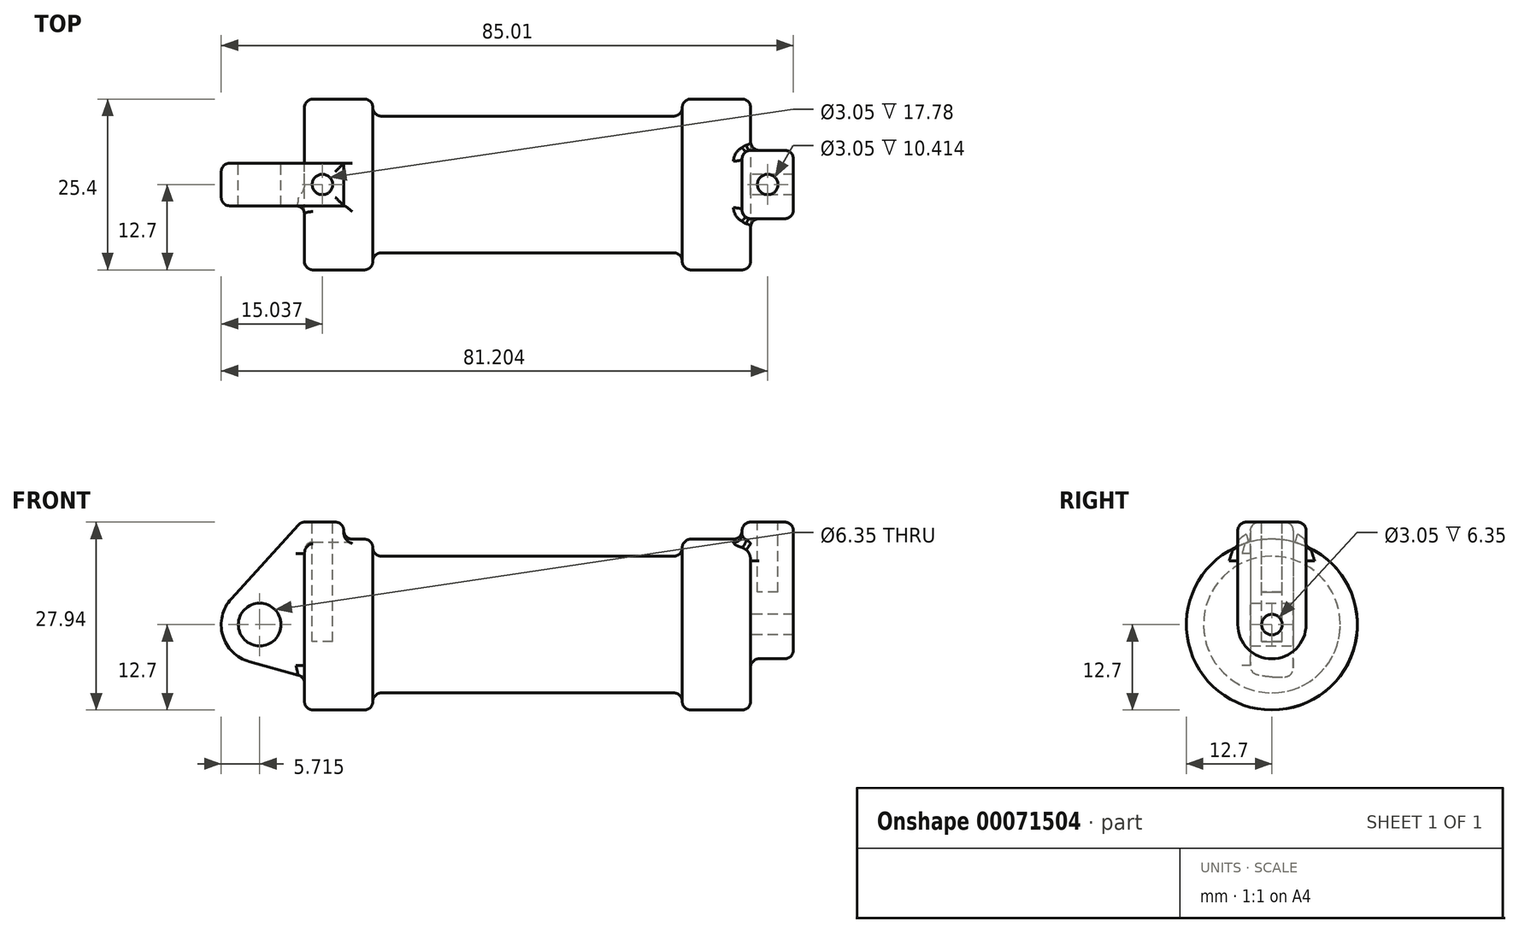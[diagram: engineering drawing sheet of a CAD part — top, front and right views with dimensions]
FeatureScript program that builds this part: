
annotation { "Feature Type Name" : "Feature", "Feature Type Description" : "" }
export const myFeature = defineFeature(function(context is Context, id is Id, definition is map)
    precondition{}
    {
        {
            var Q0;
            Q0=qCreatedBy(makeId("Front.planeOp"),FACE);
            var sketch = newSketch(context, id + "F0", { "sketchPlane" : qUnion([Q0])});
            skLineSegment(sketch, "E0", {"start": v(0, 0) * mm, "end": v(0, 12.7) * mm});
            skLineSegment(sketch, "E1", {"start": v(0, 12.7) * mm, "end": v(10.16, 12.7) * mm});
            skLineSegment(sketch, "E2", {"start": v(10.16, 12.7) * mm, "end": v(10.16, 10.16) * mm});
            skLineSegment(sketch, "E3", {"start": v(10.16, 10.16) * mm, "end": v(56.13, 10.16) * mm});
            skLineSegment(sketch, "E4", {"start": v(56.13, 10.16) * mm, "end": v(56.13, 12.7) * mm});
            skLineSegment(sketch, "E5", {"start": v(56.13, 12.7) * mm, "end": v(66.3, 12.7) * mm});
            skLineSegment(sketch, "E6", {"start": v(66.3, 12.7) * mm, "end": v(66.3, 0) * mm});
            skLineSegment(sketch, "E7", {"start": v(66.3, 0) * mm, "end": v(0, 0) * mm});
            skLineSegment(sketch, "E8", {"start": v(5.84, 15.24) * mm, "end": v(-0.5, 15.24) * mm});
            skLineSegment(sketch, "E9", {"start": v(-0.5, 15.24) * mm, "end": v(-10.88, 3.85) * mm});
            skLineSegment(sketch, "E10", {"start": v(0, 0) * mm, "end": v(-6.65, 0) * mm});
            skCircle(sketch, "E11", {"center": v(-6.65, 0) * mm, "radius": 5.72 * mm});
            skCircle(sketch, "E12", {"center": v(-6.65, 0) * mm, "radius": 3.18 * mm});
            skLineSegment(sketch, "E13", {"start": v(5.84, 15.24) * mm, "end": v(5.84, -9.4) * mm});
            skLineSegment(sketch, "E14", {"start": v(5.84, -9.4) * mm, "end": v(-8.18, -5.5) * mm});
            skSolve(sketch);
        }
        {
            var Q0;
            {var subQ0=sQuery(id+"F0.wireOp",EDGE,"E2");Q0=makeQuery(id+"F0.imprint","IMPRINT",FACE,{"disambiguationData":[TD([[makeQuery(id+"F0.imprint","IMPRINT",EDGE,{"derivedFrom":subQ0}),-1.0]])]});}
            var Q1;
            {var subQ0=sQuery(id+"F0.wireOp",EDGE,"E0");Q1=makeQuery(id+"F0.imprint","IMPRINT",FACE,{"disambiguationData":[TD([[makeQuery(id+"F0.imprint","IMPRINT",EDGE,{"derivedFrom":subQ0}),-1.0]])]});}
            var Q2;
            Q2=sQuery(id+"F0.wireOp",EDGE,"E7");
            revolve(context, id + "F1", {"entities" : qUnion([Q0, Q1]), "axis" : qUnion([Q2]), "revolveType" : RevolveType.FULL});
        }
        {
            var Q0;
            {var subQ3=sQuery(id+"F0.wireOp",EDGE,"E0");Q0=makeQuery(id+"F0.imprint","IMPRINT",FACE,{"disambiguationData":[TD([[makeQuery(id+"F0.imprint","IMPRINT",EDGE,{"derivedFrom":subQ3}),1.0]])]});}
            var Q1;
            {var subQ0=sQuery(id+"F0.wireOp",EDGE,"E14");Q1=makeQuery(id+"F0.imprint","IMPRINT",FACE,{"disambiguationData":[TD([[makeQuery(id+"F0.imprint","IMPRINT",EDGE,{"derivedFrom":subQ0}),-1.0]])]});}
            var Q2;
            {var subQ4=sQuery(id+"F0.wireOp",EDGE,"E12");Q2=makeQuery(id+"F0.imprint","IMPRINT",FACE,{"disambiguationData":[TD([[makeQuery(id+"F0.imprint","IMPRINT",EDGE,{"derivedFrom":subQ4}),-1.0]])]});}
            var Q3;
            {var subQ0=sQuery(id+"F0.wireOp",EDGE,"E0");Q3=makeQuery(id+"F0.imprint","IMPRINT",FACE,{"disambiguationData":[TD([[makeQuery(id+"F0.imprint","IMPRINT",EDGE,{"derivedFrom":subQ0}),-1.0]])]});}
            extrude(context, id + "F2", {"entities" : qUnion([Q0, Q1, Q2, Q3]), "operationType" : NewBodyOperationType.ADD, "endBound" : BoundingType.SYMMETRIC, "depth" : 6.35 * mm});
        }
        {
            var Q0;
            Q0=makeQuery(id+"F1.opRevolve","SWEPT_FACE",FACE,{"disambiguationData":[OSD([sQuery(id+"F0.wireOp",EDGE,"E6")])]});
            var sketch = newSketch(context, id + "F3", { "sketchPlane" : qUnion([Q0])});
            skCircle(sketch, "E15", {"center": v(0, 0) * mm, "radius": 1.52 * mm});
            skCircle(sketch, "E16", {"center": v(0, 0) * mm, "radius": 5.08 * mm});
            skLineSegment(sketch, "E17", {"start": v(5.08, 0) * mm, "end": v(5.08, 15.24) * mm});
            skLineSegment(sketch, "E18", {"start": v(-5.08, 0) * mm, "end": v(-5.08, 15.24) * mm});
            skLineSegment(sketch, "E19", {"start": v(-5.08, 15.24) * mm, "end": v(5.08, 15.24) * mm});
            skSolve(sketch);
        }
        {
            var Q0;
            {var subQ0=sQuery(id+"F3.wireOp",EDGE,"E19");Q0=makeQuery(id+"F3.imprint","IMPRINT",FACE,{"disambiguationData":[TD([[makeQuery(id+"F3.imprint","IMPRINT",EDGE,{"derivedFrom":subQ0}),-1.0]])]});}
            var Q1;
            {var subQ0=sQuery(id+"F3.wireOp",EDGE,"E17");var subQ1=sQuery(id+"F3.wireOp",EDGE,"E16");var subQ2=makeQuery(id+"F3.imprint","INTERSECT",VERTEX,{"derivedFrom":[subQ1,subQ0]});Q1=makeQuery(id+"F3.imprint","IMPRINT",FACE,{"disambiguationData":[TD([[makeQuery(id+"F3.imprint","IMPRINT",EDGE,{"disambiguationData":[TD([[subQ2,-1.0]])],"derivedFrom":subQ1}),-1.0]])]});}
            var Q2;
            Q2=makeQuery(id+"F3.imprint","IMPRINT",FACE,{"disambiguationData":[TD([[makeQuery(id+"F3.imprint","IMPRINT",EDGE,{"derivedFrom":sQuery(id+"F3.wireOp",EDGE,"E15")}),-1.0]])]});
            extrude(context, id + "F4", {"entities" : qUnion([Q0, Q1, Q2]), "operationType" : NewBodyOperationType.ADD, "depth" : 6.35 * mm});
        }
        {
            var Q0;
            Q0 = qSketchRegion(id + "F3", true);
            extrude(context, id + "F5", {"entities" : qUnion([Q0]), "operationType" : NewBodyOperationType.ADD, "oppositeDirection" : true, "depth" : 1.27 * mm});
        }
        {
            var Q0;
            Q0=makeQuery(id+"F2.opExtrude","SWEPT_FACE",FACE,{"disambiguationData":[OSD([sQuery(id+"F0.wireOp",EDGE,"E8")])]});
            var sketch = newSketch(context, id + "F6", { "sketchPlane" : qUnion([Q0])});
            skLineSegment(sketch, "E20", {"start": v(2.67, 3.18) * mm, "end": v(2.67, -3.18) * mm, "construction": true});
            skLineSegment(sketch, "E21", {"start": v(5.84, 0) * mm, "end": v(-0.5, 0) * mm});
            skCircle(sketch, "E22", {"center": v(2.67, 0) * mm, "radius": 1.52 * mm});
            skSolve(sketch);
        }
        {
            var Q0;
            {var subQ0=sQuery(id+"F6.wireOp",EDGE,"E22");var subQ1=sQuery(id+"F6.wireOp",EDGE,"E21");var subQ2=makeQuery(id+"F6.imprint","INTERSECT",VERTEX,{"disambiguationData":[OD(0.0)],"derivedFrom":[subQ1,subQ0]});Q0=makeQuery(id+"F6.imprint","IMPRINT",FACE,{"disambiguationData":[TD([[makeQuery(id+"F6.imprint","IMPRINT",EDGE,{"disambiguationData":[TD([[subQ2,-1.0]])],"derivedFrom":subQ1}),-1.0]])]});}
            var Q1;
            {var subQ0=sQuery(id+"F6.wireOp",EDGE,"E22");var subQ1=sQuery(id+"F6.wireOp",EDGE,"E21");var subQ2=makeQuery(id+"F6.imprint","INTERSECT",VERTEX,{"disambiguationData":[OD(0.0)],"derivedFrom":[subQ1,subQ0]});Q1=makeQuery(id+"F6.imprint","IMPRINT",FACE,{"disambiguationData":[TD([[makeQuery(id+"F6.imprint","IMPRINT",EDGE,{"disambiguationData":[TD([[subQ2,-1.0]])],"derivedFrom":subQ1}),1.0]])]});}
            extrude(context, id + "F7", {"entities" : qUnion([Q0, Q1]), "operationType" : NewBodyOperationType.REMOVE, "oppositeDirection" : true, "depth" : 17.78 * mm});
        }
        {
            var Q0;
            {var subQ0=sQuery(id+"F3.wireOp",EDGE,"E19");Q0=makeQuery(id+"F5.boolean.opBoolean","MERGE",FACE,{"derivedFrom":[makeQuery(id+"F4.opExtrude","SWEPT_FACE",FACE,{"disambiguationData":[OSD([subQ0])]}),makeQuery(id+"F5.opExtrude","SWEPT_FACE",FACE,{"disambiguationData":[OSD([subQ0])]})]});}
            var sketch = newSketch(context, id + "F8", { "sketchPlane" : qUnion([Q0])});
            skLineSegment(sketch, "E23", {"start": v(68.83, -5.08) * mm, "end": v(68.83, 5.08) * mm, "construction": true});
            skLineSegment(sketch, "E24", {"start": v(72.64, 0) * mm, "end": v(65.02, 0) * mm});
            skCircle(sketch, "E25", {"center": v(68.83, 0) * mm, "radius": 1.52 * mm});
            skSolve(sketch);
        }
        {
            var Q0;
            {var subQ0=sQuery(id+"F8.wireOp",EDGE,"E25");var subQ1=sQuery(id+"F8.wireOp",EDGE,"E24");var subQ2=makeQuery(id+"F8.imprint","INTERSECT",VERTEX,{"disambiguationData":[OD(0.0)],"derivedFrom":[subQ1,subQ0]});Q0=makeQuery(id+"F8.imprint","IMPRINT",FACE,{"disambiguationData":[TD([[makeQuery(id+"F8.imprint","IMPRINT",EDGE,{"disambiguationData":[TD([[subQ2,-1.0]])],"derivedFrom":subQ1}),-1.0]])]});}
            var Q1;
            {var subQ0=sQuery(id+"F8.wireOp",EDGE,"E25");var subQ1=sQuery(id+"F8.wireOp",EDGE,"E24");var subQ2=makeQuery(id+"F8.imprint","INTERSECT",VERTEX,{"disambiguationData":[OD(0.0)],"derivedFrom":[subQ1,subQ0]});Q1=makeQuery(id+"F8.imprint","IMPRINT",FACE,{"disambiguationData":[TD([[makeQuery(id+"F8.imprint","IMPRINT",EDGE,{"disambiguationData":[TD([[subQ2,-1.0]])],"derivedFrom":subQ1}),1.0]])]});}
            extrude(context, id + "F9", {"entities" : qUnion([Q0, Q1]), "operationType" : NewBodyOperationType.REMOVE, "oppositeDirection" : true, "depth" : 10.4 * mm});
        }
        {
            var Q0;
            Q0=makeQuery(id+"F1.opRevolve","SWEPT_EDGE",EDGE,{"disambiguationData":[OSD([sQuery(id+"F0.wireOp",EDGE,"E0"),sQuery(id+"F0.wireOp",EDGE,"E1")])]});
            var Q1;
            Q1=makeQuery(id+"F1.opRevolve","SWEPT_EDGE",EDGE,{"disambiguationData":[OSD([sQuery(id+"F0.wireOp",EDGE,"E1"),sQuery(id+"F0.wireOp",EDGE,"E2")])]});
            var Q2;
            Q2=makeQuery(id+"F1.opRevolve","SWEPT_EDGE",EDGE,{"disambiguationData":[OSD([sQuery(id+"F0.wireOp",EDGE,"E2"),sQuery(id+"F0.wireOp",EDGE,"E3")])]});
            var Q3;
            Q3=makeQuery(id+"F1.opRevolve","SWEPT_EDGE",EDGE,{"disambiguationData":[OSD([sQuery(id+"F0.wireOp",EDGE,"E3"),sQuery(id+"F0.wireOp",EDGE,"E4")])]});
            var Q4;
            Q4=makeQuery(id+"F1.opRevolve","SWEPT_EDGE",EDGE,{"disambiguationData":[OSD([sQuery(id+"F0.wireOp",EDGE,"E4"),sQuery(id+"F0.wireOp",EDGE,"E5")])]});
            var Q5;
            Q5=makeQuery(id+"F4.boolean.opBoolean","SPLIT",EDGE,{"disambiguationData":[OD(1.0)],"derivedFrom":makeQuery(id+"F1.opRevolve","SWEPT_EDGE",EDGE,{"disambiguationData":[OSD([sQuery(id+"F0.wireOp",EDGE,"E5"),sQuery(id+"F0.wireOp",EDGE,"E6")])]})});
            fillet(context, id + "F10", {"entities" : qUnion([Q0, Q1, Q2, Q3, Q4, Q5]), "radius" : 1.27 * mm, "tangentPropagation" : true, "allowEdgeOverflow" : false});
        }
        {
            var Q0;
            Q0=makeQuery(id+"F2.opExtrude","SWEPT_FACE",FACE,{"disambiguationData":[OSD([sQuery(id+"F0.wireOp",EDGE,"E9")])]});
            var Q1;
            Q1=makeQuery(id+"F2.opExtrude","CAP_EDGE",EDGE,{"disambiguationData":[OSD([sQuery(id+"F0.wireOp",EDGE,"E8")])],"isStart":true});
            var Q2;
            Q2=makeQuery(id+"F2.opExtrude","SWEPT_EDGE",EDGE,{"disambiguationData":[OSD([sQuery(id+"F0.wireOp",EDGE,"E8"),sQuery(id+"F0.wireOp",EDGE,"E13")])]});
            var Q3;
            Q3=makeQuery(id+"F2.opExtrude","CAP_EDGE",EDGE,{"disambiguationData":[OSD([sQuery(id+"F0.wireOp",EDGE,"E8")])],"isStart":false});
            var Q4;
            Q4=makeQuery(id+"F2.boolean.opBoolean","INTERSECT",EDGE,{"derivedFrom":[makeQuery(id+"F1.opRevolve","SWEPT_FACE",FACE,{"disambiguationData":[OSD([sQuery(id+"F0.wireOp",EDGE,"E0")])]}),makeQuery(id+"F2.opExtrude","CAP_FACE",FACE,{"disambiguationData":[OSD([sQuery(id+"F0.wireOp",EDGE,"E8"),sQuery(id+"F0.wireOp",EDGE,"E9"),sQuery(id+"F0.wireOp",EDGE,"E11"),sQuery(id+"F0.wireOp",EDGE,"E12"),sQuery(id+"F0.wireOp",EDGE,"E13"),sQuery(id+"F0.wireOp",EDGE,"E14")])],"isStart":false})]});
            var Q5;
            Q5=makeQuery(id+"F2.boolean.opBoolean","INTERSECT",EDGE,{"derivedFrom":[makeQuery(id+"F1.opRevolve","SWEPT_FACE",FACE,{"disambiguationData":[OSD([sQuery(id+"F0.wireOp",EDGE,"E1")])]}),makeQuery(id+"F2.opExtrude","SWEPT_FACE",FACE,{"disambiguationData":[OSD([sQuery(id+"F0.wireOp",EDGE,"E13")])]})]});
            fillet(context, id + "F11", {"entities" : qUnion([Q0, Q1, Q2, Q3, Q4, Q5]), "radius" : 1.27 * mm, "tangentPropagation" : true, "allowEdgeOverflow" : false});
        }
        {
            var Q0;
            {var subQ0=sQuery(id+"F3.wireOp",EDGE,"E18");var subQ1=sQuery(id+"F3.wireOp",EDGE,"E16");Q0=makeQuery(id+"F4.boolean.opBoolean","SPLIT",EDGE,{"disambiguationData":[TD([makeQuery(id+"F4.opExtrude","SWEPT_FACE",FACE,{"disambiguationData":[OSD([subQ1])]})])],"derivedFrom":makeQuery(id+"F4.opExtrude","CAP_EDGE",EDGE,{"disambiguationData":[OSD([subQ0])],"isStart":true})});}
            var Q1;
            Q1=makeQuery(id+"F4.opExtrude","CAP_EDGE",EDGE,{"disambiguationData":[OSD([sQuery(id+"F3.wireOp",EDGE,"E18")])],"isStart":false});
            var Q2;
            {var subQ0=sQuery(id+"F3.wireOp",EDGE,"E19");var subQ1=sQuery(id+"F3.wireOp",EDGE,"E18");Q2=makeQuery(id+"F5.boolean.opBoolean","MERGE",EDGE,{"derivedFrom":[makeQuery(id+"F4.opExtrude","SWEPT_EDGE",EDGE,{"disambiguationData":[OSD([subQ1,subQ0])]}),makeQuery(id+"F5.opExtrude","SWEPT_EDGE",EDGE,{"disambiguationData":[OSD([subQ1,subQ0])]})]});}
            var Q3;
            Q3=makeQuery(id+"F5.opExtrude","CAP_EDGE",EDGE,{"disambiguationData":[OSD([sQuery(id+"F3.wireOp",EDGE,"E18")])],"isStart":false});
            var Q4;
            {var subQ0=sQuery(id+"F3.wireOp",EDGE,"E18");Q4=makeQuery(id+"F10.opFillet","BLEND_EDGE",EDGE,{"blendedFrom":[makeQuery(id+"F4.boolean.opBoolean","SPLIT",EDGE,{"disambiguationData":[OD(1.0)],"derivedFrom":makeQuery(id+"F1.opRevolve","SWEPT_EDGE",EDGE,{"disambiguationData":[OSD([sQuery(id+"F0.wireOp",EDGE,"E5"),sQuery(id+"F0.wireOp",EDGE,"E6")])]})}),makeQuery(id+"F5.boolean.opBoolean","MERGE",FACE,{"derivedFrom":[makeQuery(id+"F4.opExtrude","SWEPT_FACE",FACE,{"disambiguationData":[OSD([subQ0])]}),makeQuery(id+"F5.opExtrude","SWEPT_FACE",FACE,{"disambiguationData":[OSD([subQ0])]})]})],"blendedInto":[makeQuery(id+"F5.boolean.opBoolean","MERGE",FACE,{"derivedFrom":[makeQuery(id+"F4.opExtrude","SWEPT_FACE",FACE,{"disambiguationData":[OSD([subQ0])]}),makeQuery(id+"F5.opExtrude","SWEPT_FACE",FACE,{"disambiguationData":[OSD([subQ0])]})]})]});}
            var Q5;
            Q5=makeQuery(id+"F4.opExtrude","CAP_EDGE",EDGE,{"disambiguationData":[OSD([sQuery(id+"F3.wireOp",EDGE,"E16")])],"isStart":false});
            var Q6;
            Q6=makeQuery(id+"F4.opExtrude","CAP_EDGE",EDGE,{"disambiguationData":[OSD([sQuery(id+"F3.wireOp",EDGE,"E16")])],"isStart":true});
            var Q7;
            Q7=makeQuery(id+"F4.opExtrude","CAP_EDGE",EDGE,{"disambiguationData":[OSD([sQuery(id+"F3.wireOp",EDGE,"E17")])],"isStart":false});
            var Q8;
            {var subQ0=sQuery(id+"F3.wireOp",EDGE,"E17");var subQ1=sQuery(id+"F3.wireOp",EDGE,"E16");Q8=makeQuery(id+"F4.boolean.opBoolean","SPLIT",EDGE,{"disambiguationData":[TD([makeQuery(id+"F4.opExtrude","SWEPT_FACE",FACE,{"disambiguationData":[OSD([subQ1])]})])],"derivedFrom":makeQuery(id+"F4.opExtrude","CAP_EDGE",EDGE,{"disambiguationData":[OSD([subQ0])],"isStart":true})});}
            var Q9;
            {var subQ0=sQuery(id+"F3.wireOp",EDGE,"E19");var subQ1=sQuery(id+"F3.wireOp",EDGE,"E17");Q9=makeQuery(id+"F5.boolean.opBoolean","MERGE",EDGE,{"derivedFrom":[makeQuery(id+"F4.opExtrude","SWEPT_EDGE",EDGE,{"disambiguationData":[OSD([subQ1,subQ0])]}),makeQuery(id+"F5.opExtrude","SWEPT_EDGE",EDGE,{"disambiguationData":[OSD([subQ1,subQ0])]})]});}
            var Q10;
            Q10=makeQuery(id+"F4.opExtrude","CAP_EDGE",EDGE,{"disambiguationData":[OSD([sQuery(id+"F3.wireOp",EDGE,"E19")])],"isStart":false});
            var Q11;
            {var subQ0=sQuery(id+"F3.wireOp",EDGE,"E17");Q11=makeQuery(id+"F10.opFillet","BLEND_EDGE",EDGE,{"blendedFrom":[makeQuery(id+"F4.boolean.opBoolean","SPLIT",EDGE,{"disambiguationData":[OD(1.0)],"derivedFrom":makeQuery(id+"F1.opRevolve","SWEPT_EDGE",EDGE,{"disambiguationData":[OSD([sQuery(id+"F0.wireOp",EDGE,"E5"),sQuery(id+"F0.wireOp",EDGE,"E6")])]})}),makeQuery(id+"F5.boolean.opBoolean","MERGE",FACE,{"derivedFrom":[makeQuery(id+"F4.opExtrude","SWEPT_FACE",FACE,{"disambiguationData":[OSD([subQ0])]}),makeQuery(id+"F5.opExtrude","SWEPT_FACE",FACE,{"disambiguationData":[OSD([subQ0])]})]})],"blendedInto":[makeQuery(id+"F5.boolean.opBoolean","MERGE",FACE,{"derivedFrom":[makeQuery(id+"F4.opExtrude","SWEPT_FACE",FACE,{"disambiguationData":[OSD([subQ0])]}),makeQuery(id+"F5.opExtrude","SWEPT_FACE",FACE,{"disambiguationData":[OSD([subQ0])]})]})]});}
            var Q12;
            Q12=makeQuery(id+"F5.opExtrude","CAP_EDGE",EDGE,{"disambiguationData":[OSD([sQuery(id+"F3.wireOp",EDGE,"E17")])],"isStart":false});
            var Q13;
            Q13=makeQuery(id+"F5.boolean.opBoolean","INTERSECT",EDGE,{"derivedFrom":[makeQuery(id+"F1.opRevolve","SWEPT_FACE",FACE,{"disambiguationData":[OSD([sQuery(id+"F0.wireOp",EDGE,"E5")])]}),makeQuery(id+"F5.opExtrude","CAP_FACE",FACE,{"disambiguationData":[OSD([sQuery(id+"F3.wireOp",EDGE,"E15"),sQuery(id+"F3.wireOp",EDGE,"E16"),sQuery(id+"F3.wireOp",EDGE,"E17"),sQuery(id+"F3.wireOp",EDGE,"E18"),sQuery(id+"F3.wireOp",EDGE,"E19")])],"isStart":false})]});
            var Q14;
            Q14=makeQuery(id+"F5.opExtrude","CAP_EDGE",EDGE,{"disambiguationData":[OSD([sQuery(id+"F3.wireOp",EDGE,"E19")])],"isStart":false});
            fillet(context, id + "F12", {"entities" : qUnion([Q0, Q1, Q2, Q3, Q4, Q5, Q6, Q7, Q8, Q9, Q10, Q11, Q12, Q13, Q14]), "radius" : 1.27 * mm, "tangentPropagation" : true, "allowEdgeOverflow" : false});
        }
    });
